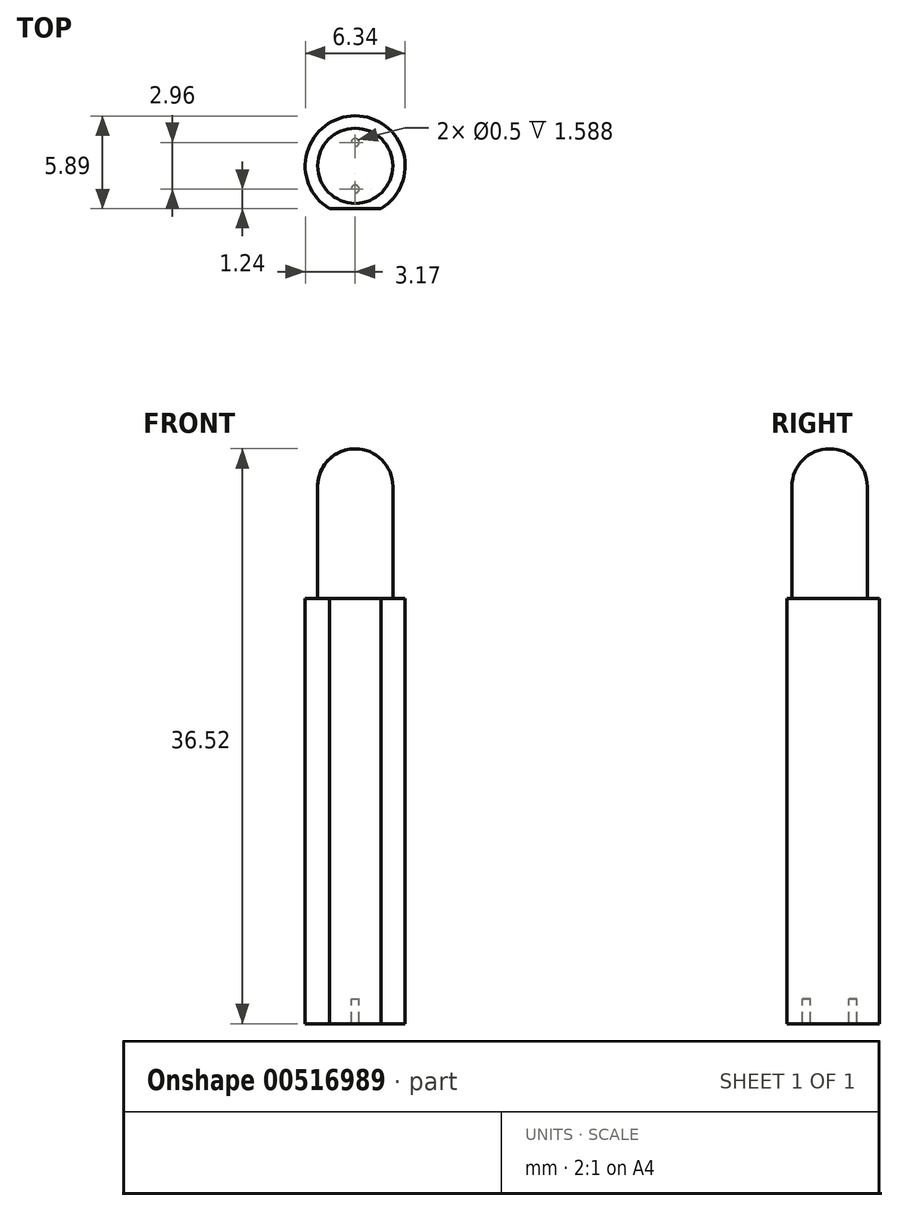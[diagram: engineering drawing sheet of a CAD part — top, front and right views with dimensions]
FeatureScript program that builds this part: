
annotation { "Feature Type Name" : "Feature", "Feature Type Description" : "" }
export const myFeature = defineFeature(function(context is Context, id is Id, definition is map)
    precondition{}
    {
        {
            var Q0;
            Q0=qCreatedBy(makeId("Top.planeOp"),FACE);
            var sketch = newSketch(context, id + "F0", { "sketchPlane" : qUnion([Q0])});
            skCircle(sketch, "E0", {"center": v(0, 0) * mm, "radius": 3.18 * mm});
            skSolve(sketch);
        }
        {
            var Q0;
            Q0 = qSketchRegion(id + "F0", true);
            extrude(context, id + "F1", {"entities" : qUnion([Q0]), "depth" : 1 / 406.4 * mm, "offsetDistance" : 25.4 * mm});
        }
        {
            var Q0;
            Q0=qCreatedBy(makeId("Front.planeOp"),FACE);
            var sketch = newSketch(context, id + "F2", { "sketchPlane" : qUnion([Q0])});
            skLineSegment(sketch, "E1", {"start": v(0, 0) * mm, "end": v(0, 9.53) * mm});
            skLineSegment(sketch, "E2", {"start": v(2.39, 0) * mm, "end": v(2.39, 7.14) * mm});
            skArc(sketch, "E3", {"start": v(2.39, 7.14) * mm, "mid": v(1.69, 8.83) * mm, "end": v(0, 9.53) * mm});
            skLineSegment(sketch, "E4", {"start": v(0, 0) * mm, "end": v(2.39, 0) * mm});
            skLineSegment(sketch, "E5.MirrorCS", {"start": v(-2.39, 0) * mm, "end": v(-2.39, 7.14) * mm});
            skArc(sketch, "E6.MirrorCS", {"start": v(-2.39, 7.14) * mm, "mid": v(-1.69, 8.83) * mm, "end": v(0, 9.53) * mm});
            skLineSegment(sketch, "E7.MirrorCS", {"start": v(0, 0) * mm, "end": v(-2.39, 0) * mm});
            skSolve(sketch);
        }
        {
            var Q0;
            Q0=qCreatedBy(makeId("Front.planeOp"),FACE);
            var sketch = newSketch(context, id + "F3", { "sketchPlane" : qUnion([Q0])});
            skLineSegment(sketch, "E8", {"start": v(0, 0) * mm, "end": v(0, 43.17) * mm});
            skSolve(sketch);
        }
        {
            var Q0;
            Q0=makeQuery(id+"F2.imprint","IMPRINT",FACE,{"disambiguationData":[TD([[makeQuery(id+"F2.imprint","IMPRINT",EDGE,{"derivedFrom":sQuery(id+"F2.wireOp",EDGE,"E1")}),1.0]])]});
            var Q1;
            Q1=sQuery(id+"F3.wireOp",EDGE,"E8");
            revolve(context, id + "F4", {"operationType" : NewBodyOperationType.ADD, "entities" : qUnion([Q0]), "axis" : qUnion([Q1]), "revolveType" : RevolveType.FULL});
        }
        {
            var Q0;
            Q0=qCreatedBy(makeId("Front.planeOp"),FACE);
            cPlane(context, id + "F5", {"entities" : qUnion([Q0]), "cplaneType" : CPlaneType.OFFSET, "offset" : 2.72 * mm, "width" : 152.4 * mm, "height" : 152.4 * mm});
        }
        {
            var Q0;
            Q0=qCreatedBy(id+"F5.planeOp",FACE);
            var sketch = newSketch(context, id + "F6", { "sketchPlane" : qUnion([Q0])});
            skLineSegment(sketch, "E9.bottom", {"start": v(-10.07, 32.52) * mm, "end": v(10.36, 32.52) * mm});
            skLineSegment(sketch, "E9.top", {"start": v(-10.07, -3.74) * mm, "end": v(10.36, -3.74) * mm});
            skLineSegment(sketch, "E9.left", {"start": v(-10.07, 32.52) * mm, "end": v(-10.07, -3.74) * mm});
            skLineSegment(sketch, "E9.right", {"start": v(10.36, 32.52) * mm, "end": v(10.36, -3.74) * mm});
            skSolve(sketch);
        }
        {
            var Q0;
            Q0 = qSketchRegion(id + "F6", true);
            extrude(context, id + "F7", {"entities" : qUnion([Q0]), "operationType" : NewBodyOperationType.REMOVE, "depth" : 10.67 * mm, "offsetDistance" : 25.4 * mm});
        }
        {
            var Q0;
            Q0=makeQuery(id+"F1.opExtrude","CAP_FACE",FACE,{"disambiguationData":[OSD([sQuery(id+"F0.wireOp",EDGE,"E0")])],"isStart":true});
            var sketch = newSketch(context, id + "F8", { "sketchPlane" : qUnion([Q0])});
            skCircle(sketch, "E10", {"center": v(0, -1.48) * mm, "radius": 0.25 * mm});
            skCircle(sketch, "E11.MirrorC", {"center": v(0, 1.48) * mm, "radius": 0.25 * mm});
            skSolve(sketch);
        }
        {
            var Q0;
            Q0 = qSketchRegion(id + "F8", true);
            extrude(context, id + "F9", {"entities" : qUnion([Q0]), "operationType" : NewBodyOperationType.ADD, "depth" : 25.4 * mm, "offsetDistance" : 25.4 * mm});
        }
        {
            var Q0;
            Q0=makeQuery(id+"F8.imprint","IMPRINT",FACE,{"disambiguationData":[TD([[makeQuery(id+"F8.imprint","IMPRINT",EDGE,{"derivedFrom":sQuery(id+"F8.wireOp",EDGE,"E11.MirrorC")}),-1.0]])]});
            extrude(context, id + "F10", {"entities" : qUnion([Q0]), "operationType" : NewBodyOperationType.ADD, "depth" : 26.99 * mm, "offsetDistance" : 25.4 * mm});
        }
    });
